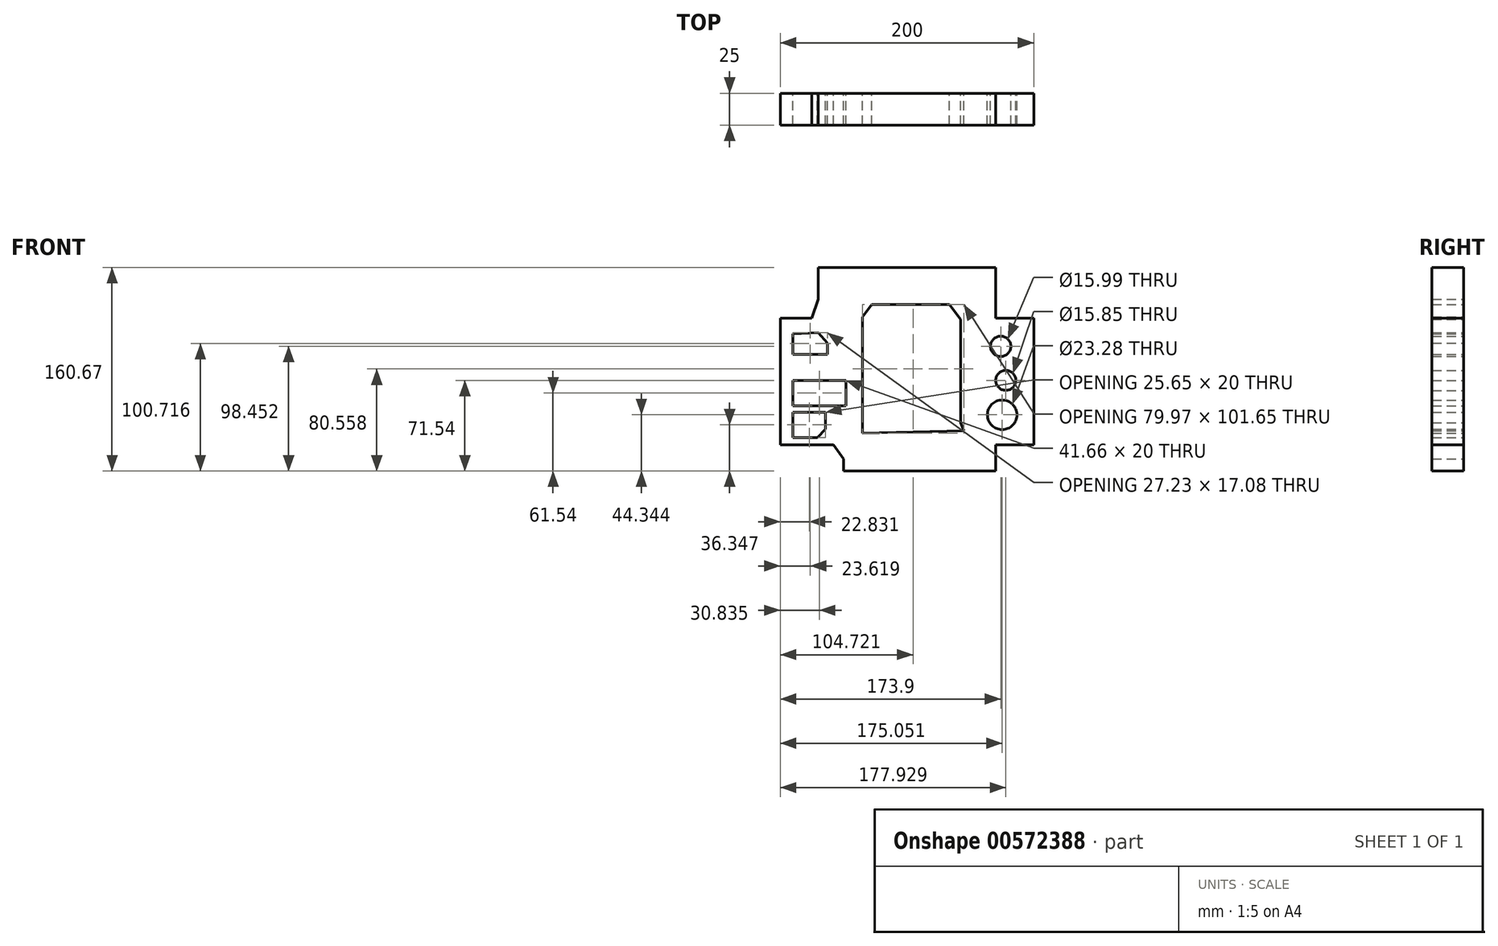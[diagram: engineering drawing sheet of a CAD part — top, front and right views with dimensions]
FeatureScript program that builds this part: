
annotation { "Feature Type Name" : "Feature", "Feature Type Description" : "" }
export const myFeature = defineFeature(function(context is Context, id is Id, definition is map)
    precondition{}
    {
        {
            var Q0;
            Q0=qCreatedBy(makeId("Front.planeOp"),FACE);
            var sketch = newSketch(context, id + "F0", { "sketchPlane" : qUnion([Q0])});
            skLineSegment(sketch, "E0", {"start": v(-98.36, 49.13) * mm, "end": v(-98.36, -50.87) * mm});
            skLineSegment(sketch, "E1", {"start": v(-98.36, -50.87) * mm, "end": v(-56.34, -50.87) * mm});
            skLineSegment(sketch, "E2", {"start": v(-56.34, -50.87) * mm, "end": v(-48.36, -61.93) * mm});
            skLineSegment(sketch, "E3", {"start": v(-48.36, -61.93) * mm, "end": v(-48.36, -71.54) * mm});
            skLineSegment(sketch, "E4", {"start": v(-48.36, -71.54) * mm, "end": v(71.64, -71.54) * mm});
            skLineSegment(sketch, "E5", {"start": v(71.64, -71.54) * mm, "end": v(71.64, -50.87) * mm});
            skLineSegment(sketch, "E6", {"start": v(71.64, -50.87) * mm, "end": v(101.64, -50.87) * mm});
            skLineSegment(sketch, "E7", {"start": v(101.64, -50.87) * mm, "end": v(101.64, 49.13) * mm});
            skLineSegment(sketch, "E8", {"start": v(101.64, 49.13) * mm, "end": v(71.64, 49.13) * mm});
            skLineSegment(sketch, "E9", {"start": v(71.64, 49.13) * mm, "end": v(71.64, 89.13) * mm});
            skLineSegment(sketch, "E10", {"start": v(71.64, 89.13) * mm, "end": v(-68.36, 89.13) * mm});
            skLineSegment(sketch, "E11", {"start": v(-68.36, 89.13) * mm, "end": v(-68.36, 64.04) * mm});
            skLineSegment(sketch, "E12", {"start": v(-68.36, 64.04) * mm, "end": v(-73.64, 49.13) * mm});
            skLineSegment(sketch, "E13", {"start": v(-73.64, 49.13) * mm, "end": v(-98.36, 49.13) * mm});
            skLineSegment(sketch, "E14", {"start": v(-88.36, 36.6) * mm, "end": v(-88.36, 20.63) * mm});
            skLineSegment(sketch, "E15", {"start": v(-88.36, 20.63) * mm, "end": v(-61.13, 20.63) * mm});
            skLineSegment(sketch, "E16", {"start": v(-61.13, 20.63) * mm, "end": v(-61.13, 29.49) * mm});
            skLineSegment(sketch, "E17", {"start": v(-61.13, 29.49) * mm, "end": v(-68.39, 37.72) * mm});
            skLineSegment(sketch, "E18", {"start": v(-68.39, 37.72) * mm, "end": v(-88.36, 36.6) * mm});
            skLineSegment(sketch, "E19.bottom", {"start": v(-88.36, 0) * mm, "end": v(-46.7, 0) * mm});
            skLineSegment(sketch, "E19.top", {"start": v(-88.36, -20) * mm, "end": v(-46.7, -20) * mm});
            skLineSegment(sketch, "E19.left", {"start": v(-88.36, 0) * mm, "end": v(-88.36, -20) * mm});
            skLineSegment(sketch, "E19.right", {"start": v(-46.7, 0) * mm, "end": v(-46.7, -20) * mm});
            skLineSegment(sketch, "E20", {"start": v(-88.36, -25.2) * mm, "end": v(-62.7, -25.2) * mm});
            skLineSegment(sketch, "E21", {"start": v(-62.7, -25.2) * mm, "end": v(-62.7, -38.42) * mm});
            skLineSegment(sketch, "E22", {"start": v(-62.7, -38.42) * mm, "end": v(-69, -45.2) * mm});
            skLineSegment(sketch, "E23", {"start": v(-69, -45.2) * mm, "end": v(-88.36, -45.2) * mm});
            skLineSegment(sketch, "E24", {"start": v(-88.36, -45.2) * mm, "end": v(-88.36, -25.2) * mm});
            skLineSegment(sketch, "E25", {"start": v(-26.36, 59.84) * mm, "end": v(35.1, 59.84) * mm});
            skLineSegment(sketch, "E26", {"start": v(35.1, 59.84) * mm, "end": v(43.82, 48.22) * mm});
            skLineSegment(sketch, "E27", {"start": v(43.82, 48.22) * mm, "end": v(43.82, -33.58) * mm});
            skLineSegment(sketch, "E28", {"start": v(43.82, -33.58) * mm, "end": v(46.35, -39.64) * mm});
            skLineSegment(sketch, "E29", {"start": v(-26.36, 59.84) * mm, "end": v(-33.62, 50.16) * mm});
            skLineSegment(sketch, "E30", {"start": v(-33.62, 50.16) * mm, "end": v(-33.62, -41.8) * mm});
            skLineSegment(sketch, "E31", {"start": v(-33.62, -41.8) * mm, "end": v(46.35, -39.64) * mm});
            skCircle(sketch, "E32", {"center": v(75.54, 26.91) * mm, "radius": 8 * mm});
            skCircle(sketch, "E33", {"center": v(79.57, 0) * mm, "radius": 7.92 * mm});
            skCircle(sketch, "E34", {"center": v(76.7, -27.2) * mm, "radius": 11.64 * mm});
            skSolve(sketch);
        }
        {
            var Q0;
            Q0 = qSketchRegion(id + "F0", true);
            extrude(context, id + "F1", {"entities" : qUnion([Q0]), "depth" : 25 * mm, "offsetDistance" : 25 * mm});
        }
        {
            var Q0;
            Q0 = qSketchRegion(id + "F0", true);
            extrude(context, id + "F2", {"entities" : qUnion([Q0]), "operationType" : NewBodyOperationType.ADD, "depth" : 25 * mm, "offsetDistance" : 25 * mm});
        }
    });
